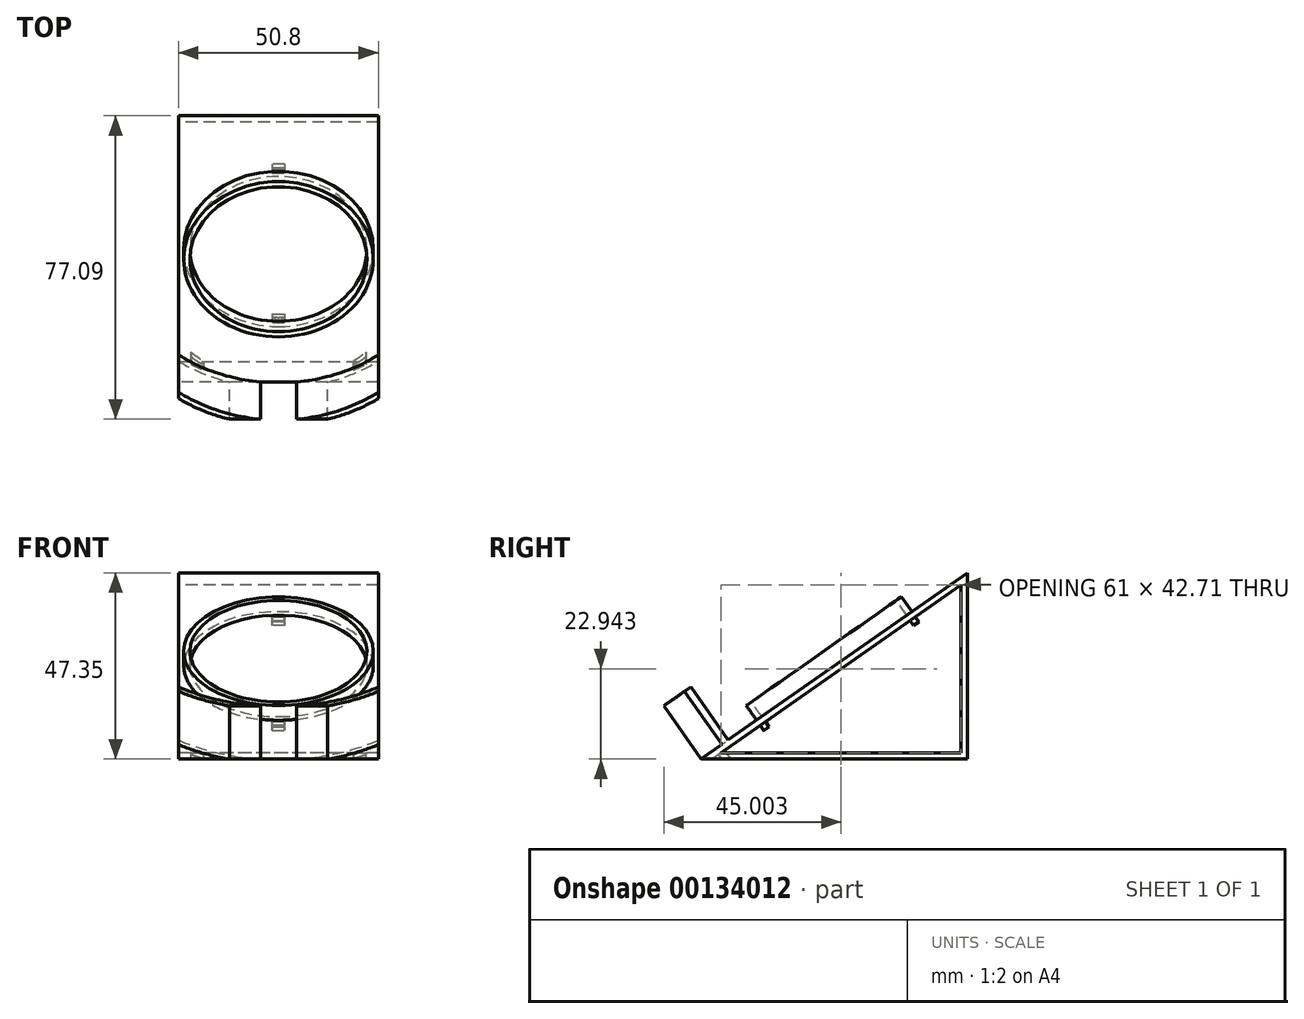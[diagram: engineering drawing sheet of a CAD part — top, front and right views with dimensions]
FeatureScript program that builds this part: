
annotation { "Feature Type Name" : "Feature", "Feature Type Description" : "" }
export const myFeature = defineFeature(function(context is Context, id is Id, definition is map)
    precondition{}
    {
        {
            var Q0;
            Q0=qCreatedBy(makeId("Right.planeOp"),FACE);
            var sketch = newSketch(context, id + "F0", { "sketchPlane" : qUnion([Q0])});
            skLineSegment(sketch, "E0", {"start": v(0, 0) * mm, "end": v(0, 47.35) * mm});
            skLineSegment(sketch, "E1", {"start": v(0, 47.35) * mm, "end": v(-67.62, 0) * mm});
            skLineSegment(sketch, "E2", {"start": v(-67.62, 0) * mm, "end": v(0, 0) * mm});
            skLineSegment(sketch, "E3.0", {"start": v(-1.59, 44.3) * mm, "end": v(-62.59, 1.59) * mm});
            skLineSegment(sketch, "E3.1", {"start": v(-1.59, 1.59) * mm, "end": v(-1.59, 44.3) * mm});
            skLineSegment(sketch, "E3.2", {"start": v(-62.59, 1.59) * mm, "end": v(-1.59, 1.59) * mm});
            skSolve(sketch);
        }
        {
            var Q0;
            Q0 = qSketchRegion(id + "F0", true);
            extrude(context, id + "F1", {"entities" : qUnion([Q0]), "depth" : 50.8 * mm});
        }
        {
            var Q0;
            Q0=makeQuery(id+"F1.opExtrude","SWEPT_FACE",FACE,{"disambiguationData":[OSD([sQuery(id+"F0.wireOp",EDGE,"E1")])]});
            var sketch = newSketch(context, id + "F2", { "sketchPlane" : qUnion([Q0])});
            skLineSegment(sketch, "E4", {"start": v(25.4, 27.16) * mm, "end": v(25.4, -55.4) * mm, "construction": true});
            skLineSegment(sketch, "E5", {"start": v(0, -14.12) * mm, "end": v(50.8, -14.12) * mm, "construction": true});
            skCircle(sketch, "E6", {"center": v(25.4, -14.12) * mm, "radius": 22.48 * mm});
            skCircle(sketch, "E7.0", {"center": v(25.4, -14.12) * mm, "radius": 24.07 * mm});
            skLineSegment(sketch, "E8.0", {"start": v(26.99, 9.9) * mm, "end": v(26.99, 8.3) * mm});
            skLineSegment(sketch, "E9.0", {"start": v(23.81, 9.9) * mm, "end": v(23.81, 8.3) * mm});
            skLineSegment(sketch, "E10.trimOffspring", {"start": v(23.81, -36.54) * mm, "end": v(23.81, -38.13) * mm});
            skLineSegment(sketch, "E11.trimOffspring", {"start": v(26.99, -36.54) * mm, "end": v(26.99, -38.13) * mm});
            skArc(sketch, "E12", {"start": v(0, -46.97) * mm, "mid": v(9.83, -52.62) * mm, "end": v(20.81, -55.4) * mm});
            skArc(sketch, "E13", {"start": v(-0.57, -46.52) * mm, "mid": v(-0.29, -46.75) * mm, "end": v(0, -46.97) * mm});
            skArc(sketch, "E14", {"start": v(29.99, -55.4) * mm, "mid": v(40.97, -52.62) * mm, "end": v(50.8, -46.97) * mm});
            skArc(sketch, "E15", {"start": v(50.8, -46.97) * mm, "mid": v(25.76, 27.41) * mm, "end": v(-0.57, -46.52) * mm});
            skArc(sketch, "E16.0", {"start": v(0, -48.96) * mm, "mid": v(6.2, -52.72) * mm, "end": v(12.93, -55.4) * mm});
            skArc(sketch, "E17.0", {"start": v(37.87, -55.4) * mm, "mid": v(44.6, -52.72) * mm, "end": v(50.8, -48.96) * mm});
            skLineSegment(sketch, "E18", {"start": v(50.8, -46.97) * mm, "end": v(50.8, -48.96) * mm});
            skLineSegment(sketch, "E19.0", {"start": v(47.63, -49.2) * mm, "end": v(47.63, -51.06) * mm});
            skLineSegment(sketch, "E20.0", {"start": v(44.45, -51.02) * mm, "end": v(44.45, -52.8) * mm});
            skLineSegment(sketch, "E21", {"start": v(0, -46.97) * mm, "end": v(0, -48.96) * mm});
            skLineSegment(sketch, "E22.0", {"start": v(3.18, -49.2) * mm, "end": v(3.18, -51.06) * mm});
            skLineSegment(sketch, "E23.0", {"start": v(6.35, -51.02) * mm, "end": v(6.35, -52.8) * mm});
            skSolve(sketch);
        }
        {
            var Q0;
            {var subQ0=sQuery(id+"F2.wireOp",EDGE,"E10.trimOffspring");Q0=makeQuery(id+"F2.imprint","IMPRINT",FACE,{"disambiguationData":[TD([[makeQuery(id+"F2.imprint","IMPRINT",EDGE,{"derivedFrom":subQ0}),1.0]])]});}
            var Q1;
            {var subQ0=sQuery(id+"F2.wireOp",EDGE,"E8.0");Q1=makeQuery(id+"F2.imprint","IMPRINT",FACE,{"disambiguationData":[TD([[makeQuery(id+"F2.imprint","IMPRINT",EDGE,{"derivedFrom":subQ0}),-1.0]])]});}
            extrude(context, id + "F3", {"entities" : qUnion([Q0, Q1]), "operationType" : NewBodyOperationType.REMOVE, "endBound" : BoundingType.UP_TO_NEXT, "oppositeDirection" : true, "depth" : 25.4 * mm});
        }
        {
            var Q0;
            {var subQ0=sQuery(id+"F2.wireOp",EDGE,"E8.0");Q0=makeQuery(id+"F2.imprint","IMPRINT",FACE,{"disambiguationData":[TD([[makeQuery(id+"F2.imprint","IMPRINT",EDGE,{"derivedFrom":subQ0}),-1.0]])]});}
            var Q1;
            {var subQ0=sQuery(id+"F2.wireOp",EDGE,"E10.trimOffspring");Q1=makeQuery(id+"F2.imprint","IMPRINT",FACE,{"disambiguationData":[TD([[makeQuery(id+"F2.imprint","IMPRINT",EDGE,{"derivedFrom":subQ0}),1.0]])]});}
            extrude(context, id + "F4", {"entities" : qUnion([Q0, Q1]), "oppositeDirection" : true, "depth" : 3.17 * mm});
        }
        {
            var Q0;
            {var subQ0=sQuery(id+"F2.wireOp",EDGE,"E8.0");Q0=makeQuery(id+"F2.imprint","IMPRINT",FACE,{"disambiguationData":[TD([[makeQuery(id+"F2.imprint","IMPRINT",EDGE,{"derivedFrom":subQ0}),1.0]])]});}
            var Q1;
            {var subQ0=sQuery(id+"F2.wireOp",EDGE,"E10.trimOffspring");Q1=makeQuery(id+"F2.imprint","IMPRINT",FACE,{"disambiguationData":[TD([[makeQuery(id+"F2.imprint","IMPRINT",EDGE,{"derivedFrom":subQ0}),1.0]])]});}
            var Q2;
            {var subQ0=sQuery(id+"F2.wireOp",EDGE,"E9.0");Q2=makeQuery(id+"F2.imprint","IMPRINT",FACE,{"disambiguationData":[TD([[makeQuery(id+"F2.imprint","IMPRINT",EDGE,{"derivedFrom":subQ0}),-1.0]])]});}
            var Q3;
            {var subQ0=sQuery(id+"F2.wireOp",EDGE,"E8.0");Q3=makeQuery(id+"F2.imprint","IMPRINT",FACE,{"disambiguationData":[TD([[makeQuery(id+"F2.imprint","IMPRINT",EDGE,{"derivedFrom":subQ0}),-1.0]])]});}
            extrude(context, id + "F5", {"entities" : qUnion([Q0, Q1, Q2, Q3]), "operationType" : NewBodyOperationType.ADD, "depth" : 4.57 * mm});
        }
        {
            var Q0;
            {var subQ0=sQuery(id+"F2.wireOp",EDGE,"E19.0");Q0=makeQuery(id+"F2.imprint","IMPRINT",FACE,{"disambiguationData":[TD([[makeQuery(id+"F2.imprint","IMPRINT",EDGE,{"derivedFrom":subQ0}),-1.0]])]});}
            var Q1;
            {var subQ0=sQuery(id+"F2.wireOp",EDGE,"E22.0");Q1=makeQuery(id+"F2.imprint","IMPRINT",FACE,{"disambiguationData":[TD([[makeQuery(id+"F2.imprint","IMPRINT",EDGE,{"derivedFrom":subQ0}),1.0]])]});}
            extrude(context, id + "F6", {"entities" : qUnion([Q0, Q1]), "operationType" : NewBodyOperationType.REMOVE, "endBound" : BoundingType.UP_TO_NEXT, "oppositeDirection" : true, "depth" : 25.4 * mm});
        }
        {
            var Q0;
            {var subQ0=sQuery(id+"F2.wireOp",EDGE,"E19.0");Q0=makeQuery(id+"F2.imprint","IMPRINT",FACE,{"disambiguationData":[TD([[makeQuery(id+"F2.imprint","IMPRINT",EDGE,{"derivedFrom":subQ0}),-1.0]])]});}
            var Q1;
            {var subQ0=sQuery(id+"F2.wireOp",EDGE,"E22.0");Q1=makeQuery(id+"F2.imprint","IMPRINT",FACE,{"disambiguationData":[TD([[makeQuery(id+"F2.imprint","IMPRINT",EDGE,{"derivedFrom":subQ0}),1.0]])]});}
            extrude(context, id + "F7", {"entities" : qUnion([Q0, Q1]), "oppositeDirection" : true, "depth" : 1.59 * mm});
        }
        {
            var Q0;
            {var subQ0=sQuery(id+"F2.wireOp",EDGE,"E21");Q0=makeQuery(id+"F2.imprint","IMPRINT",FACE,{"disambiguationData":[TD([[makeQuery(id+"F2.imprint","IMPRINT",EDGE,{"derivedFrom":subQ0}),1.0]])]});}
            var Q1;
            {var subQ0=sQuery(id+"F2.wireOp",EDGE,"E22.0");Q1=makeQuery(id+"F2.imprint","IMPRINT",FACE,{"disambiguationData":[TD([[makeQuery(id+"F2.imprint","IMPRINT",EDGE,{"derivedFrom":subQ0}),1.0]])]});}
            var Q2;
            {var subQ3=sQuery(id+"F2.wireOp",EDGE,"E23.0");Q2=makeQuery(id+"F2.imprint","IMPRINT",FACE,{"disambiguationData":[TD([[makeQuery(id+"F2.imprint","IMPRINT",EDGE,{"derivedFrom":subQ3}),1.0]])]});}
            var Q3;
            {var subQ3=sQuery(id+"F2.wireOp",EDGE,"E20.0");Q3=makeQuery(id+"F2.imprint","IMPRINT",FACE,{"disambiguationData":[TD([[makeQuery(id+"F2.imprint","IMPRINT",EDGE,{"derivedFrom":subQ3}),-1.0]])]});}
            var Q4;
            {var subQ0=sQuery(id+"F2.wireOp",EDGE,"E19.0");Q4=makeQuery(id+"F2.imprint","IMPRINT",FACE,{"disambiguationData":[TD([[makeQuery(id+"F2.imprint","IMPRINT",EDGE,{"derivedFrom":subQ0}),-1.0]])]});}
            var Q5;
            {var subQ0=sQuery(id+"F2.wireOp",EDGE,"E18");Q5=makeQuery(id+"F2.imprint","IMPRINT",FACE,{"disambiguationData":[TD([[makeQuery(id+"F2.imprint","IMPRINT",EDGE,{"derivedFrom":subQ0}),-1.0]])]});}
            extrude(context, id + "F8", {"entities" : qUnion([Q0, Q1, Q2, Q3, Q4, Q5]), "operationType" : NewBodyOperationType.ADD, "depth" : 16.5 * mm});
        }
    });
